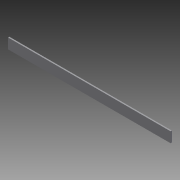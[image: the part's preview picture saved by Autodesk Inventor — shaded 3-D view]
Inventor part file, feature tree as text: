
AUTODESK INVENTOR PART (.ipt)
format: ipt  version: 2011 (Build 150239000, 239)  size: 64,512 bytes
history: native  units: in
note: dims shown in document units (in); Inventor stores cm internally (conversion verified against a paired STEP export)
features: extrude x1, sketch x1
ambient origin geometry x8: Origin, YZ Plane, XZ Plane, XY Plane, X Axis, Y Axis, Z Axis, Center Point
bodies: Solid1 (feature_tree)
feature tree (2):
  extrude  "Extrusion1"  Depth=1.0in
  sketch  "Sketch1"  dims[d0=15.748in d1=1.0in d2=0.125in d3=0.0in]
